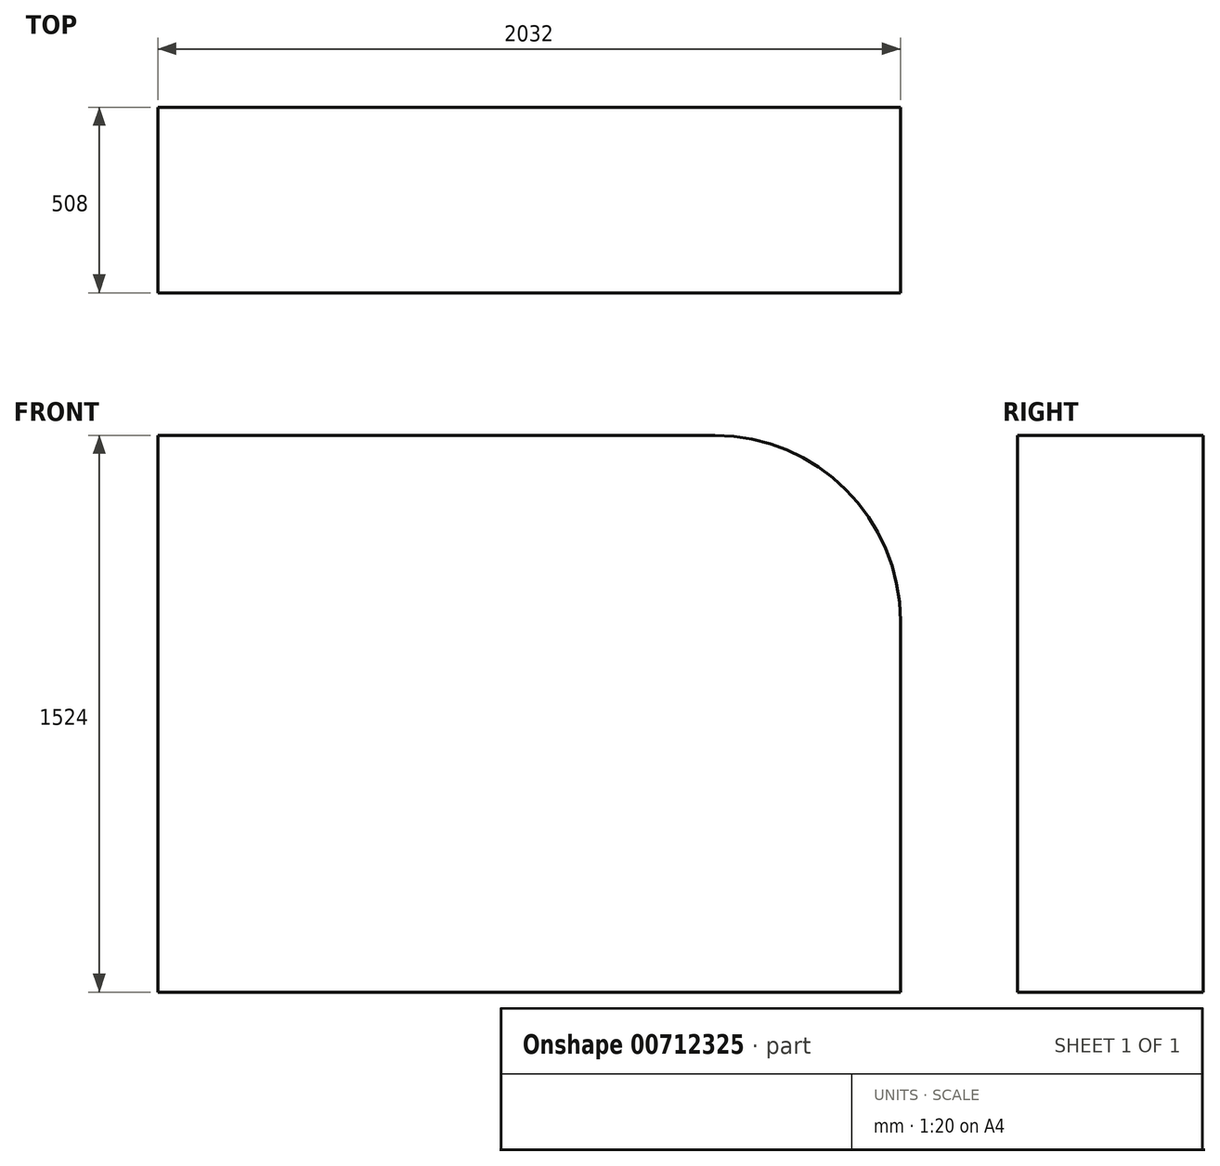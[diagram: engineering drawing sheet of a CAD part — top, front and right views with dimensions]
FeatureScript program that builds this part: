
annotation { "Feature Type Name" : "Feature", "Feature Type Description" : "" }
export const myFeature = defineFeature(function(context is Context, id is Id, definition is map)
    precondition{}
    {
        {
            var Q0;
            Q0=qCreatedBy(makeId("Front.planeOp"),FACE);
            var sketch = newSketch(context, id + "F0", { "sketchPlane" : qUnion([Q0])});
            skLineSegment(sketch, "E0.bottom", {"start": v(1016, 762) * mm, "end": v(-1016, 762) * mm});
            skLineSegment(sketch, "E0.top", {"start": v(1016, -762) * mm, "end": v(-1016, -762) * mm});
            skLineSegment(sketch, "E0.left", {"start": v(1016, 762) * mm, "end": v(1016, -762) * mm});
            skLineSegment(sketch, "E0.right", {"start": v(-1016, 762) * mm, "end": v(-1016, -762) * mm});
            skPoint(sketch, "E0.middle", {"position": v(0, 0) * mm});
            skSolve(sketch);
        }
        {
            var Q0;
            Q0 = qSketchRegion(id + "F0", true);
            extrude(context, id + "F1", {"entities" : qUnion([Q0]), "endBound" : BoundingType.SYMMETRIC, "depth" : 508 * mm, "offsetDistance" : 25.4 * mm});
        }
        {
            var Q0;
            Q0=makeQuery(id+"F1.opExtrude","SWEPT_EDGE",EDGE,{"disambiguationData":[OSD([sQuery(id+"F0.wireOp",EDGE,"E0.bottom"),sQuery(id+"F0.wireOp",EDGE,"E0.left")])]});
            fillet(context, id + "F2", {"entities" : qUnion([Q0]), "radius" : 508 * mm, "tangentPropagation" : true, "allowEdgeOverflow" : false});
        }
    });
